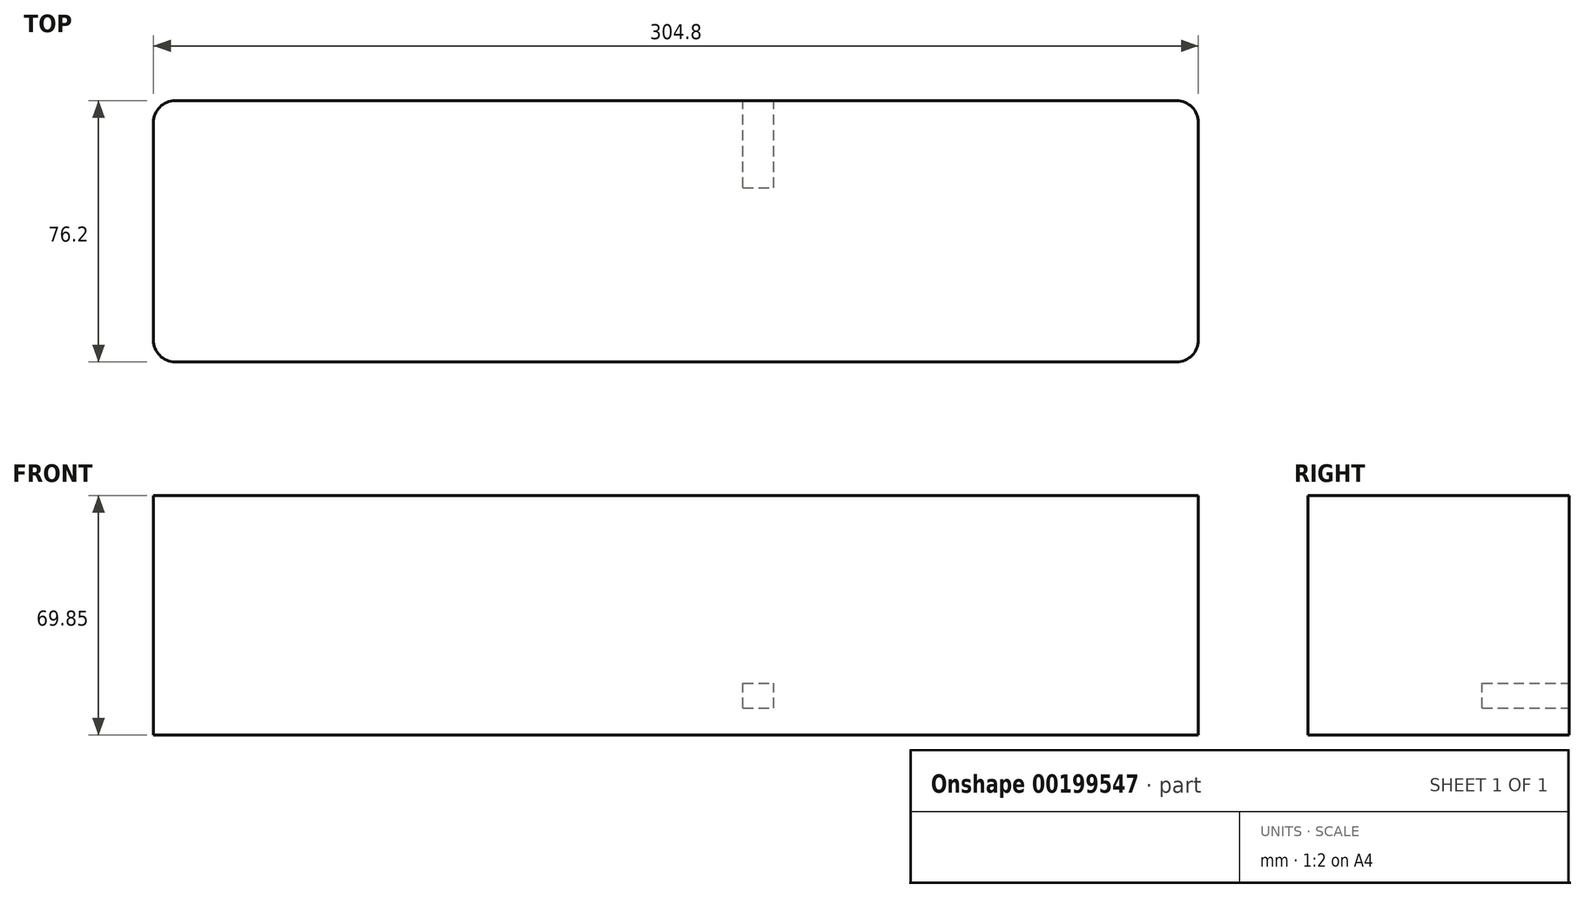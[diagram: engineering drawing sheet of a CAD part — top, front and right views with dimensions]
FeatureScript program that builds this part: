
annotation { "Feature Type Name" : "Feature", "Feature Type Description" : "" }
export const myFeature = defineFeature(function(context is Context, id is Id, definition is map)
    precondition{}
    {
        {
            var Q0;
            Q0=qCreatedBy(makeId("Top.planeOp"),FACE);
            var sketch = newSketch(context, id + "F4", { "sketchPlane" : qUnion([Q0])});
            skLineSegment(sketch, "E0.bottom", {"start": v(146.05, -38.1) * mm, "end": v(-146.05, -38.1) * mm});
            skLineSegment(sketch, "E0.top", {"start": v(146.05, 38.1) * mm, "end": v(-146.05, 38.1) * mm});
            skLineSegment(sketch, "E0.left", {"start": v(152.4, -31.75) * mm, "end": v(152.4, 31.75) * mm});
            skLineSegment(sketch, "E0.right", {"start": v(-152.4, -31.75) * mm, "end": v(-152.4, 31.75) * mm});
            skPoint(sketch, "E0.middle", {"position": v(0, 0) * mm});
            skPoint(sketch, "E1.visualSharp", {"position": v(-152.4, 38.1) * mm});
            skArc(sketch, "E1.filletArc", {"start": v(-146.05, 38.1) * mm, "mid": v(-150.54, 36.24) * mm, "end": v(-152.4, 31.75) * mm});
            skPoint(sketch, "E2.visualSharp", {"position": v(-152.4, -38.1) * mm});
            skArc(sketch, "E2.filletArc", {"start": v(-152.4, -31.75) * mm, "mid": v(-150.54, -36.24) * mm, "end": v(-146.05, -38.1) * mm});
            skPoint(sketch, "E3.visualSharp", {"position": v(152.4, -38.1) * mm});
            skArc(sketch, "E3.filletArc", {"start": v(146.05, -38.1) * mm, "mid": v(150.54, -36.24) * mm, "end": v(152.4, -31.75) * mm});
            skPoint(sketch, "E4.visualSharp", {"position": v(152.4, 38.1) * mm});
            skArc(sketch, "E4.filletArc", {"start": v(152.4, 31.75) * mm, "mid": v(150.54, 36.24) * mm, "end": v(146.05, 38.1) * mm});
            skSolve(sketch);
        }
        {
            var Q0;
            Q0=makeQuery(id+"F4.imprint","IMPRINT",FACE,{"disambiguationData":[TD([[makeQuery(id+"F4.imprint","IMPRINT",EDGE,{"derivedFrom":sQuery(id+"F4.wireOp",EDGE,"E0.bottom")}),-1.0]])]});
            extrude(context, id + "F5", {"entities" : qUnion([Q0]), "depth" : 6.35 * mm});
        }
        {
            var Q0;
            Q0=makeQuery(id+"F5.opExtrude","CAP_FACE",FACE,{"disambiguationData":[OSD([sQuery(id+"F4.wireOp",EDGE,"E0.bottom"),sQuery(id+"F4.wireOp",EDGE,"E0.top"),sQuery(id+"F4.wireOp",EDGE,"E0.left"),sQuery(id+"F4.wireOp",EDGE,"E0.right"),sQuery(id+"F4.wireOp",EDGE,"E1.filletArc"),sQuery(id+"F4.wireOp",EDGE,"E2.filletArc"),sQuery(id+"F4.wireOp",EDGE,"E3.filletArc"),sQuery(id+"F4.wireOp",EDGE,"E4.filletArc")])],"isStart":false});
            var sketch = newSketch(context, id + "F0", { "sketchPlane" : qUnion([Q0])});
            skSolve(sketch);
        }
        {
            var Q0;
            Q0=makeQuery(id+"F0.imprint","IMPRINT",FACE,{"disambiguationData":[TD([[makeQuery(id+"F0.imprint","IMPRINT",EDGE,{"derivedFrom":makeQuery(id+"F5.opExtrude","CAP_EDGE",EDGE,{"disambiguationData":[OSD([sQuery(id+"F4.wireOp",EDGE,"E0.bottom")])],"isStart":false})}),-1.0]])]});
            extrude(context, id + "F1", {"entities" : qUnion([Q0]), "operationType" : NewBodyOperationType.ADD, "depth" : 63.5 * mm});
        }
        {
            var Q0;
            {var subQ0=sQuery(id+"F4.wireOp",EDGE,"E0.top");Q0=makeQuery(id+"F1.boolean.opBoolean","MERGE",FACE,{"derivedFrom":[makeQuery(id+"F5.opExtrude","SWEPT_FACE",FACE,{"disambiguationData":[OSD([subQ0])]}),makeQuery(id+"F1.opExtrude","SWEPT_FACE",FACE,{"disambiguationData":[OSD([subQ0])]})]});}
            var sketch = newSketch(context, id + "F2", { "sketchPlane" : qUnion([Q0])});
            skLineSegment(sketch, "E5.bottom", {"start": v(-19.53, 7.87) * mm, "end": v(-28.49, 7.87) * mm});
            skLineSegment(sketch, "E5.top", {"start": v(-19.53, 15.06) * mm, "end": v(-28.49, 15.06) * mm});
            skLineSegment(sketch, "E5.left", {"start": v(-19.53, 7.87) * mm, "end": v(-19.53, 15.06) * mm});
            skLineSegment(sketch, "E5.right", {"start": v(-28.49, 7.87) * mm, "end": v(-28.49, 15.06) * mm});
            skPoint(sketch, "E5.middle", {"position": v(-24, 11.47) * mm});
            skLineSegment(sketch, "E6", {"start": v(-24, 11.47) * mm, "end": v(-10.5, 11.47) * mm, "construction": true});
            skLineSegment(sketch, "E7.bottom", {"start": v(-14.82, 7.83) * mm, "end": v(-6.18, 7.83) * mm});
            skLineSegment(sketch, "E7.top", {"start": v(-14.82, 15.1) * mm, "end": v(-6.18, 15.1) * mm});
            skLineSegment(sketch, "E7.left", {"start": v(-14.82, 7.83) * mm, "end": v(-14.82, 15.1) * mm});
            skLineSegment(sketch, "E7.right", {"start": v(-6.18, 7.83) * mm, "end": v(-6.18, 15.1) * mm});
            skPoint(sketch, "E7.middle", {"position": v(-10.5, 11.47) * mm});
            skSolve(sketch);
        }
        {
            var Q0;
            Q0=makeQuery(id+"F2.imprint","IMPRINT",FACE,{"disambiguationData":[TD([[makeQuery(id+"F2.imprint","IMPRINT",EDGE,{"derivedFrom":sQuery(id+"F2.wireOp",EDGE,"E5.bottom")}),-1.0]])]});
            extrude(context, id + "F3", {"entities" : qUnion([Q0]), "operationType" : NewBodyOperationType.REMOVE, "oppositeDirection" : true, "depth" : 25.4 * mm});
        }
    });
